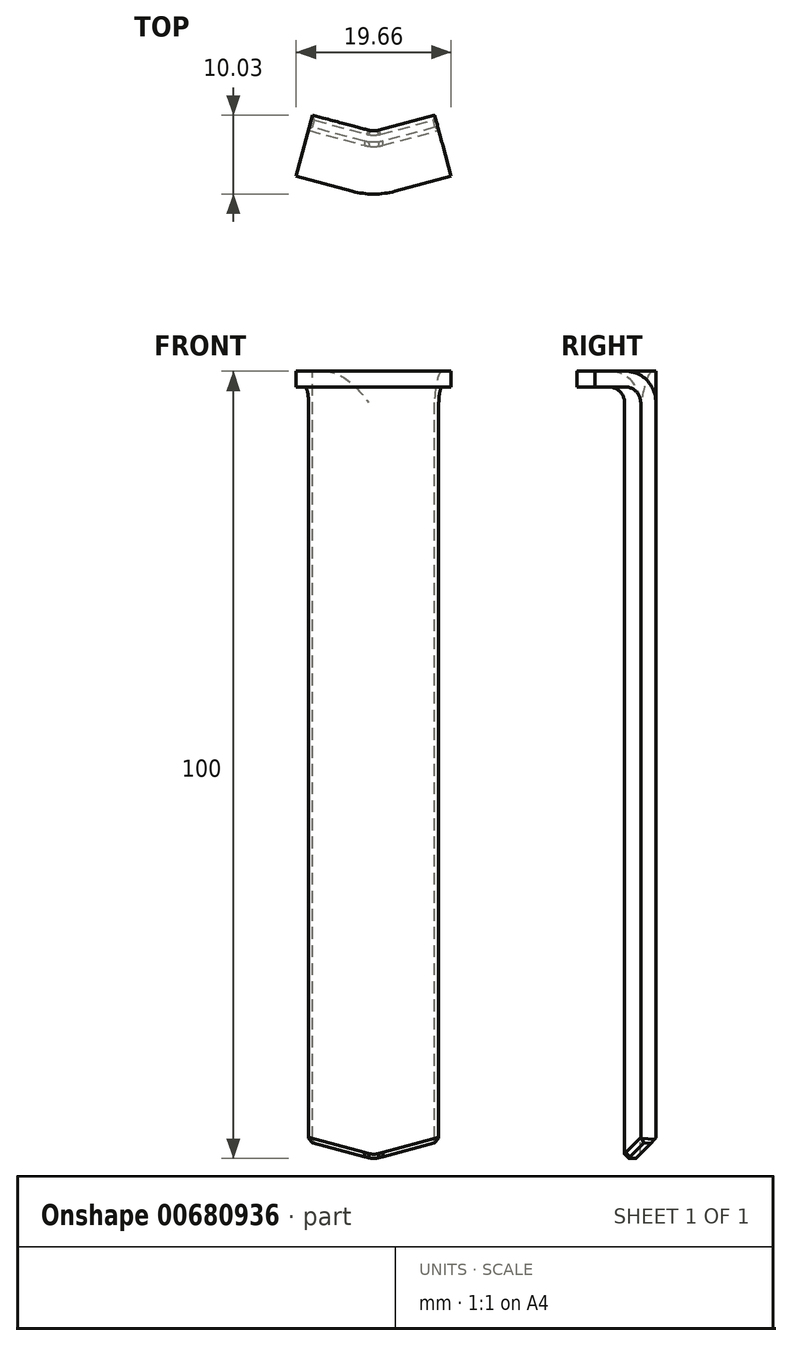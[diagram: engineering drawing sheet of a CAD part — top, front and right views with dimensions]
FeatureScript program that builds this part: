
annotation { "Feature Type Name" : "Feature", "Feature Type Description" : "" }
export const myFeature = defineFeature(function(context is Context, id is Id, definition is map)
    precondition{}
    {
        {
            var Q0;
            Q0=qCreatedBy(makeId("Top.planeOp"),FACE);
            var sketch = newSketch(context, id + "F0", { "sketchPlane" : qUnion([Q0])});
            skLineSegment(sketch, "E0", {"start": v(0, 7.62) * mm, "end": v(0, -7.78) * mm, "construction": true});
            skCircle(sketch, "E1", {"center": v(0, 0) * mm, "radius": 6 * mm, "construction": true});
            skLineSegment(sketch, "E2", {"start": v(6.45, 0) * mm, "end": v(-6.54, 0) * mm, "construction": true});
            skArc(sketch, "E3", {"start": v(-0.65, 0.09) * mm, "mid": v(0, 0) * mm, "end": v(0.65, 0.09) * mm});
            skLineSegment(sketch, "E4", {"start": v(-7.75, 1.99) * mm, "end": v(-0.65, 0.09) * mm});
            skLineSegment(sketch, "E5", {"start": v(0.65, 0.09) * mm, "end": v(7.75, 1.99) * mm});
            skLineSegment(sketch, "E6.0", {"start": v(1.16, -1.85) * mm, "end": v(8.27, 0.06) * mm});
            skArc(sketch, "E6.1", {"start": v(-1.16, -1.85) * mm, "mid": v(0, -2) * mm, "end": v(1.16, -1.85) * mm});
            skLineSegment(sketch, "E6.2", {"start": v(-8.27, 0.06) * mm, "end": v(-1.16, -1.85) * mm});
            skLineSegment(sketch, "E7", {"start": v(-7.75, 1.99) * mm, "end": v(-8.27, 0.06) * mm});
            skLineSegment(sketch, "E8", {"start": v(7.75, 1.99) * mm, "end": v(8.27, 0.06) * mm});
            skSolve(sketch);
        }
        {
            var Q0;
            Q0 = qSketchRegion(id + "F0", true);
            extrude(context, id + "F1", {"entities" : qUnion([Q0]), "oppositeDirection" : true, "depth" : 100 * mm, "offsetDistance" : 25 * mm});
        }
        {
            var Q0;
            Q0=qCreatedBy(makeId("Top.planeOp"),FACE);
            var sketch = newSketch(context, id + "F2", { "sketchPlane" : qUnion([Q0])});
            skLineSegment(sketch, "E9", {"start": v(-0.02, 7.61) * mm, "end": v(-0.02, -7.79) * mm, "construction": true});
            skCircle(sketch, "E10", {"center": v(0.01, -0.05) * mm, "radius": 6 * mm, "construction": true});
            skLineSegment(sketch, "E11", {"start": v(6.43, 0) * mm, "end": v(-6.56, 0) * mm, "construction": true});
            skArc(sketch, "E12", {"start": v(-0.67, 0.08) * mm, "mid": v(-0.02, 0) * mm, "end": v(0.63, 0.08) * mm});
            skLineSegment(sketch, "E13", {"start": v(-7.75, 1.98) * mm, "end": v(-0.67, 0.08) * mm});
            skLineSegment(sketch, "E14", {"start": v(0.63, 0.08) * mm, "end": v(7.75, 1.99) * mm});
            skLineSegment(sketch, "E15", {"start": v(7.75, 1.99) * mm, "end": v(9.83, -5.77) * mm});
            skLineSegment(sketch, "E16.0", {"start": v(2.7, -7.68) * mm, "end": v(9.83, -5.77) * mm});
            skArc(sketch, "E16.1", {"start": v(-2.73, -7.68) * mm, "mid": v(-0.01, -8.04) * mm, "end": v(2.7, -7.68) * mm});
            skLineSegment(sketch, "E16.2", {"start": v(-9.83, -5.78) * mm, "end": v(-2.73, -7.68) * mm});
            skLineSegment(sketch, "E17", {"start": v(-7.75, 1.98) * mm, "end": v(-9.83, -5.78) * mm});
            skSolve(sketch);
        }
        {
            var Q0;
            Q0 = qSketchRegion(id + "F2", true);
            extrude(context, id + "F3", {"entities" : qUnion([Q0]), "operationType" : NewBodyOperationType.ADD, "oppositeDirection" : true, "depth" : 2 * mm, "offsetDistance" : 25 * mm});
        }
        {
            var Q0;
            Q0=makeQuery(id+"F3.boolean.opBoolean","INTERSECT",EDGE,{"derivedFrom":[makeQuery(id+"F1.opExtrude","SWEPT_FACE",FACE,{"disambiguationData":[OSD([sQuery(id+"F0.wireOp",EDGE,"E6.2")])]}),makeQuery(id+"F3.opExtrude","CAP_FACE",FACE,{"disambiguationData":[OSD([sQuery(id+"F2.wireOp",EDGE,"E12"),sQuery(id+"F2.wireOp",EDGE,"E13"),sQuery(id+"F2.wireOp",EDGE,"E14"),sQuery(id+"F2.wireOp",EDGE,"E15"),sQuery(id+"F2.wireOp",EDGE,"E16.0"),sQuery(id+"F2.wireOp",EDGE,"E16.1"),sQuery(id+"F2.wireOp",EDGE,"E16.2"),sQuery(id+"F2.wireOp",EDGE,"E17")])],"isStart":false})]});
            fillet(context, id + "F4", {"entities" : qUnion([Q0]), "radius" : 2 * mm, "tangentPropagation" : true, "allowEdgeOverflow" : false});
        }
        {
            var Q0;
            Q0=makeQuery(id+"F1.opExtrude","CAP_EDGE",EDGE,{"disambiguationData":[OSD([sQuery(id+"F0.wireOp",EDGE,"E5")])],"isStart":true});
            fillet(context, id + "F5", {"entities" : qUnion([Q0]), "radius" : 4 * mm, "tangentPropagation" : true, "allowEdgeOverflow" : false});
        }
        {
            var Q0;
            Q0=qCreatedBy(makeId("Front.planeOp"),FACE);
            var sketch = newSketch(context, id + "F6", { "sketchPlane" : qUnion([Q0])});
            skLineSegment(sketch, "E18", {"start": v(0, -101.89) * mm, "end": v(0, -91.78) * mm, "construction": true});
            skLineSegment(sketch, "E19", {"start": v(-10.83, -97.19) * mm, "end": v(-0.65, -99.91) * mm});
            skLineSegment(sketch, "E20", {"start": v(0.65, -99.91) * mm, "end": v(10.83, -97.19) * mm});
            skArc(sketch, "E21", {"start": v(-0.65, -99.91) * mm, "mid": v(0, -100) * mm, "end": v(0.65, -99.91) * mm});
            skLineSegment(sketch, "E22", {"start": v(-10.83, -97.19) * mm, "end": v(-12.58, -103.7) * mm});
            skLineSegment(sketch, "E23", {"start": v(-12.58, -103.7) * mm, "end": v(-0.6, -106.91) * mm});
            skLineSegment(sketch, "E24", {"start": v(-0.6, -106.91) * mm, "end": v(12.42, -102.43) * mm});
            skLineSegment(sketch, "E25", {"start": v(12.42, -102.43) * mm, "end": v(10.83, -97.19) * mm});
            skSolve(sketch);
        }
        {
            var Q0;
            Q0 = qSketchRegion(id + "F6", true);
            extrude(context, id + "F7", {"entities" : qUnion([Q0]), "operationType" : NewBodyOperationType.REMOVE, "oppositeDirection" : true, "depth" : 50 * mm, "offsetDistance" : 25 * mm, "symmetric" : true});
        }
        {
            var Q0;
            Q0=makeQuery(id+"F7.boolean.opBoolean","INTERSECT",EDGE,{"derivedFrom":[makeQuery(id+"F1.opExtrude","SWEPT_FACE",FACE,{"disambiguationData":[OSD([sQuery(id+"F0.wireOp",EDGE,"E6.2")])]}),makeQuery(id+"F7.opExtrude","SWEPT_FACE",FACE,{"disambiguationData":[OSD([sQuery(id+"F6.wireOp",EDGE,"E19")])]})]});
            var Q1;
            Q1=makeQuery(id+"F7.boolean.opBoolean","INTERSECT",EDGE,{"derivedFrom":[makeQuery(id+"F1.opExtrude","SWEPT_FACE",FACE,{"disambiguationData":[OSD([sQuery(id+"F0.wireOp",EDGE,"E4")])]}),makeQuery(id+"F7.opExtrude","SWEPT_FACE",FACE,{"disambiguationData":[OSD([sQuery(id+"F6.wireOp",EDGE,"E19")])]})]});
            var Q2;
            Q2=makeQuery(id+"F7.boolean.opBoolean","INTERSECT",EDGE,{"derivedFrom":[makeQuery(id+"F3.boolean.opBoolean","MERGE",FACE,{"derivedFrom":[makeQuery(id+"F1.opExtrude","SWEPT_FACE",FACE,{"disambiguationData":[OSD([sQuery(id+"F0.wireOp",EDGE,"E7")])]}),makeQuery(id+"F3.opExtrude","SWEPT_FACE",FACE,{"disambiguationData":[OSD([sQuery(id+"F2.wireOp",EDGE,"E17")])]})]}),makeQuery(id+"F7.opExtrude","SWEPT_FACE",FACE,{"disambiguationData":[OSD([sQuery(id+"F6.wireOp",EDGE,"E19")])]})]});
            var Q3;
            Q3=makeQuery(id+"F7.boolean.opBoolean","INTERSECT",EDGE,{"derivedFrom":[makeQuery(id+"F3.boolean.opBoolean","MERGE",FACE,{"derivedFrom":[makeQuery(id+"F1.opExtrude","SWEPT_FACE",FACE,{"disambiguationData":[OSD([sQuery(id+"F0.wireOp",EDGE,"E8")])]}),makeQuery(id+"F3.opExtrude","SWEPT_FACE",FACE,{"disambiguationData":[OSD([sQuery(id+"F2.wireOp",EDGE,"E15")])]})]}),makeQuery(id+"F7.opExtrude","SWEPT_FACE",FACE,{"disambiguationData":[OSD([sQuery(id+"F6.wireOp",EDGE,"E20")])]})]});
            chamfer(context, id + "F8", {"entities" : qUnion([Q0, Q1, Q2, Q3]), "width" : 0.5 * mm, "tangentPropagation" : true});
        }
    });
